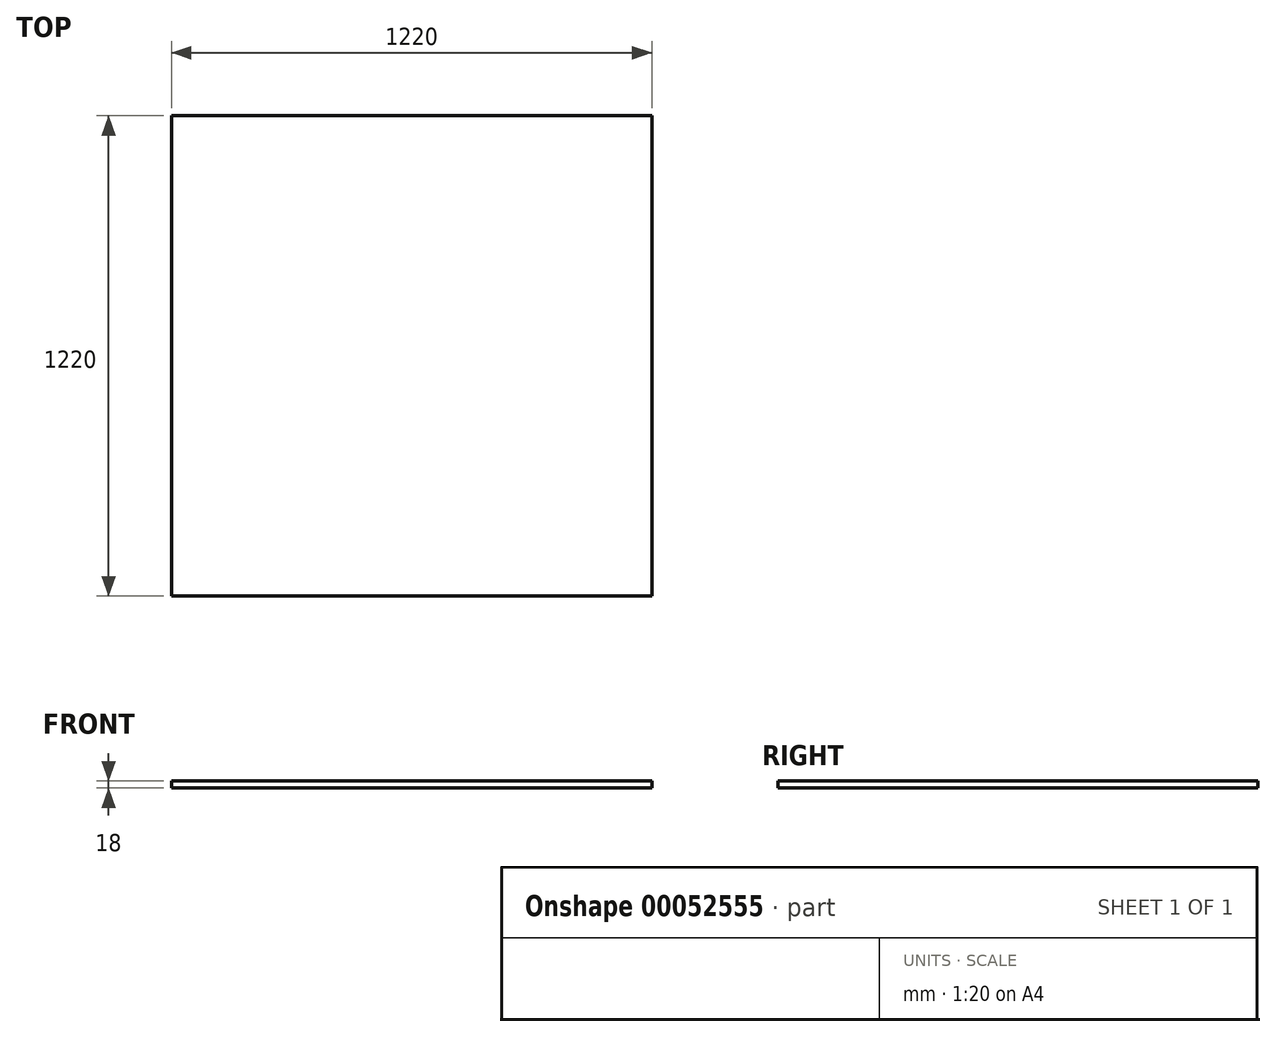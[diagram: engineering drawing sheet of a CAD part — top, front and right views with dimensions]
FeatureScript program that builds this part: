
annotation { "Feature Type Name" : "Feature", "Feature Type Description" : "" }
export const myFeature = defineFeature(function(context is Context, id is Id, definition is map)
    precondition{}
    {
        {
            var Q0;
            Q0=qCreatedBy(makeId("Top.planeOp"),FACE);
            var sketch = newSketch(context, id + "F0", { "sketchPlane" : qUnion([Q0])});
            skLineSegment(sketch, "E0.bottom", {"start": v(-610, 0) * mm, "end": v(610, 0) * mm});
            skLineSegment(sketch, "E0.top", {"start": v(-610, 1220) * mm, "end": v(610, 1220) * mm});
            skLineSegment(sketch, "E0.left", {"start": v(-610, 0) * mm, "end": v(-610, 1220) * mm});
            skLineSegment(sketch, "E0.right", {"start": v(610, 0) * mm, "end": v(610, 1220) * mm});
            skLineSegment(sketch, "E1", {"start": v(0, 0) * mm, "end": v(0, 499.27) * mm, "construction": true});
            skSolve(sketch);
        }
        {
            var Q0;
            Q0=makeQuery(id+"F0.imprint","IMPRINT",FACE,{"disambiguationData":[TD([[makeQuery(id+"F0.imprint","IMPRINT",EDGE,{"derivedFrom":sQuery(id+"F0.wireOp",EDGE,"E0.bottom")}),1.0]])]});
            extrude(context, id + "F1", {"entities" : qUnion([Q0]), "flatOperationType" : FlatOperationType.REMOVE, "offsetDistance" : 25 * mm, "depth" : 18 * mm, "domain" : OperationDomain.MODEL});
        }
    });
